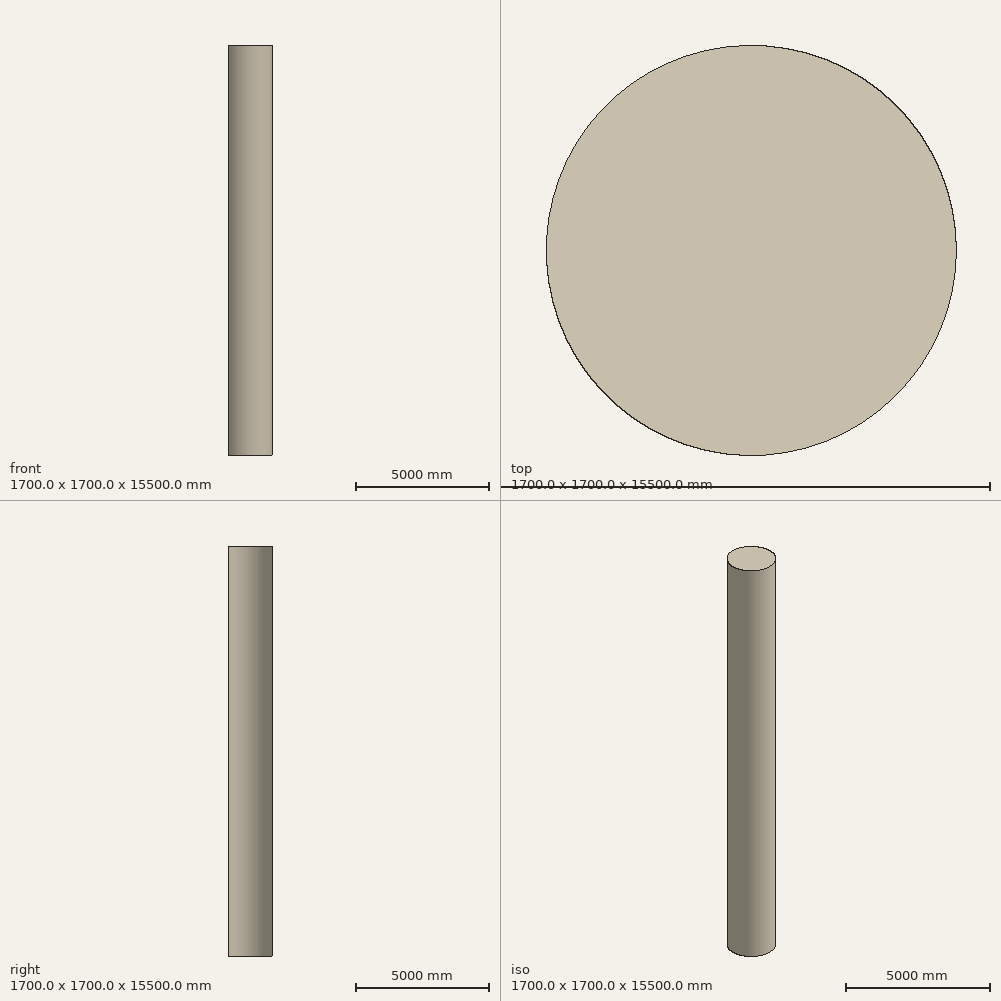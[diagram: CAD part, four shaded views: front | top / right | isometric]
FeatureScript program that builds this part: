
annotation { "Feature Type Name" : "Feature", "Feature Type Description" : "" }
export const myFeature = defineFeature(function(context is Context, id is Id, definition is map)
    precondition{}
    {
        {
            var Q0;
            Q0=qCreatedBy(makeId("Top.planeOp"),FACE);
            var sketch = newSketch(context, id + "F0", { "sketchPlane" : qUnion([Q0])});
            skCircle(sketch, "E0", {"center": v(51.52, 0) * mm, "radius": 850 * mm});
            skSolve(sketch);
        }
        {
            var Q0;
            Q0=makeQuery(id+"F0.imprint","IMPRINT",FACE,{"disambiguationData":[TD([[makeQuery(id+"F0.imprint","IMPRINT",EDGE,{"derivedFrom":sQuery(id+"F0.wireOp",EDGE,"E0")}),1.0]])]});
            extrude(context, id + "F1", {"entities" : qUnion([Q0]), "depth" : 15500 * mm, "offsetDistance" : 25.4 * mm});
        }
    });
